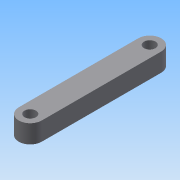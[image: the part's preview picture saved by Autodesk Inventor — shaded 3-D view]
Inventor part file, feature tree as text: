
AUTODESK INVENTOR PART (.ipt)
format: ipt  version: 2015 (Build 190159000, 159)  size: 78,848 bytes
history: native  units: mm
features: other x1, extrude x1, sketch x1
ambient origin geometry x8: Origin, YZ Plane, XZ Plane, XY Plane, X Axis, Y Axis, Z Axis, Center Point
bodies: Body1 (feature_tree)
feature tree (3):
  other  "實體1"
  extrude  "擠出1"  Depth=13.02mm
  sketch  "草圖1"
